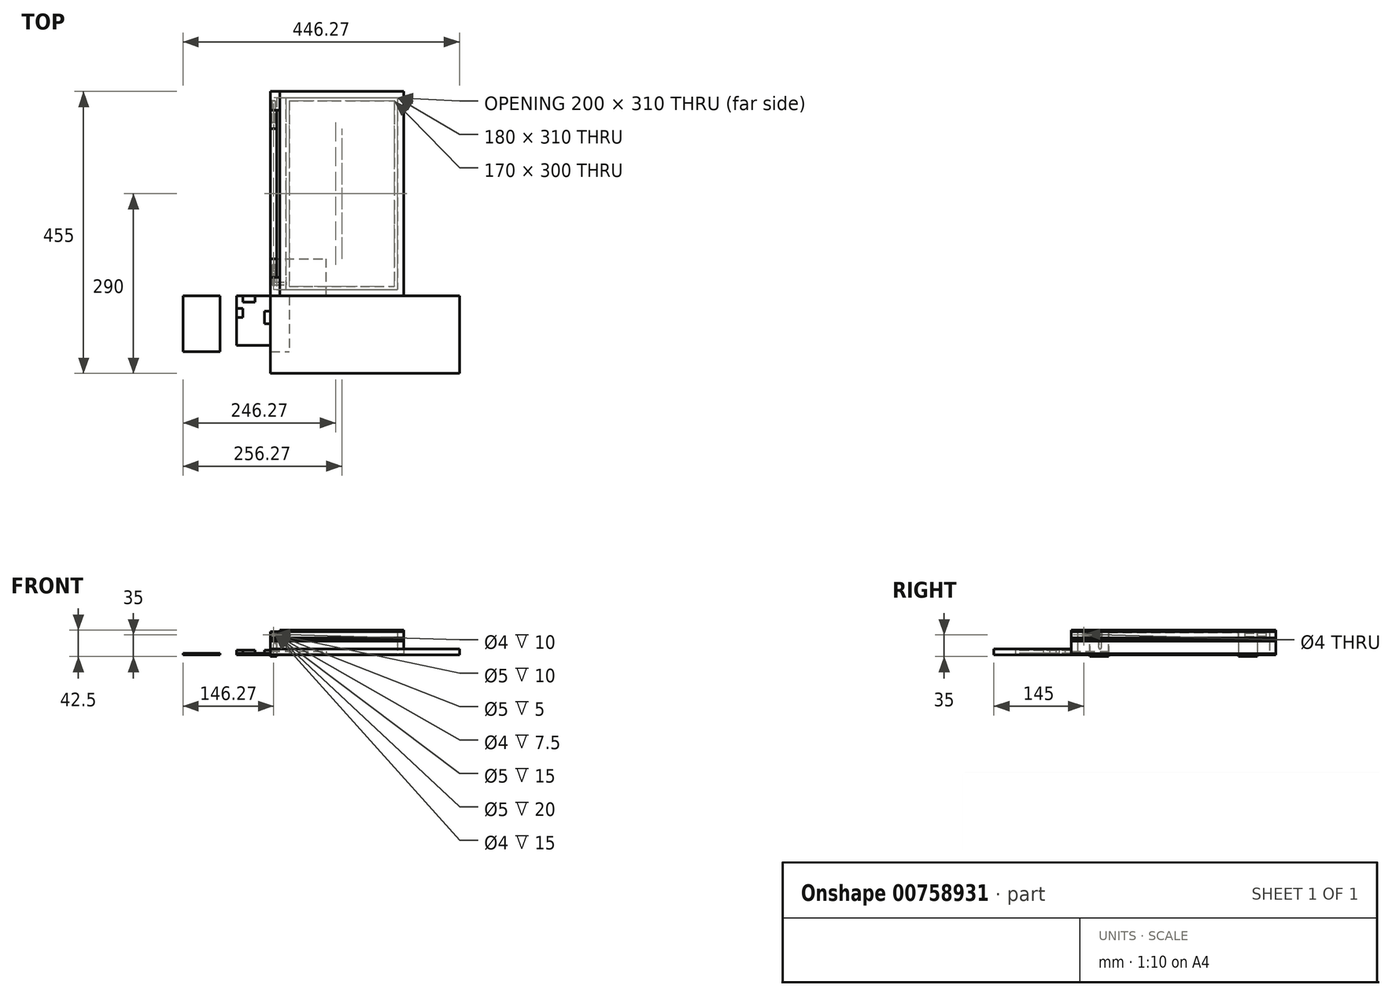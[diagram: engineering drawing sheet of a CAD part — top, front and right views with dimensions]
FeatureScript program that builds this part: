
annotation { "Feature Type Name" : "Feature", "Feature Type Description" : "" }
export const myFeature = defineFeature(function(context is Context, id is Id, definition is map)
    precondition{}
    {
        {
            var Q0;
            Q0=qCreatedBy(makeId("Top.planeOp"),FACE);
            var sketch = newSketch(context, id + "F0", { "sketchPlane" : qUnion([Q0])});
            skLineSegment(sketch, "E0.bottom", {"start": v(0, 0) * mm, "end": v(215, 0) * mm});
            skLineSegment(sketch, "E0.top", {"start": v(0, 330) * mm, "end": v(215, 330) * mm});
            skLineSegment(sketch, "E0.left", {"start": v(0, 0) * mm, "end": v(0, 330) * mm});
            skLineSegment(sketch, "E0.right", {"start": v(215, 0) * mm, "end": v(215, 330) * mm});
            skSolve(sketch);
        }
        {
            var Q0;
            Q0=makeQuery(id+"F0.imprint","IMPRINT",FACE,{"disambiguationData":[TD([[makeQuery(id+"F0.imprint","IMPRINT",EDGE,{"derivedFrom":sQuery(id+"F0.wireOp",EDGE,"E0.bottom")}),1.0]])]});
            extrude(context, id + "F1", {"entities" : qUnion([Q0]), "depth" : 2.5 * mm, "offsetDistance" : 25 * mm});
        }
        {
            var Q0;
            Q0=makeQuery(id+"F1.opExtrude","CAP_FACE",FACE,{"disambiguationData":[OSD([sQuery(id+"F0.wireOp",EDGE,"E0.bottom"),sQuery(id+"F0.wireOp",EDGE,"E0.top"),sQuery(id+"F0.wireOp",EDGE,"E0.left"),sQuery(id+"F0.wireOp",EDGE,"E0.right")])],"isStart":false});
            var sketch = newSketch(context, id + "F2", { "sketchPlane" : qUnion([Q0])});
            skLineSegment(sketch, "E1", {"start": v(215, 0) * mm, "end": v(215, 10) * mm, "construction": true});
            skLineSegment(sketch, "E2", {"start": v(215, 10) * mm, "end": v(205, 10) * mm, "construction": true});
            skLineSegment(sketch, "E3", {"start": v(0, 330) * mm, "end": v(0, 320) * mm, "construction": true});
            skLineSegment(sketch, "E4", {"start": v(0, 320) * mm, "end": v(10, 320) * mm, "construction": true});
            skLineSegment(sketch, "E5.bottom", {"start": v(10, 320) * mm, "end": v(205, 320) * mm});
            skLineSegment(sketch, "E5.top", {"start": v(10, 10) * mm, "end": v(205, 10) * mm});
            skLineSegment(sketch, "E5.left", {"start": v(10, 320) * mm, "end": v(10, 10) * mm});
            skLineSegment(sketch, "E5.right", {"start": v(205, 320) * mm, "end": v(205, 10) * mm});
            skLineSegment(sketch, "E6.bottom", {"start": v(0, 0) * mm, "end": v(215, 0) * mm});
            skLineSegment(sketch, "E6.top", {"start": v(0, 330) * mm, "end": v(215, 330) * mm});
            skLineSegment(sketch, "E6.left", {"start": v(0, 0) * mm, "end": v(0, 330) * mm});
            skLineSegment(sketch, "E6.right", {"start": v(215, 0) * mm, "end": v(215, 330) * mm});
            skSolve(sketch);
        }
        {
            var Q0;
            Q0=qSketchRegion(id+"F2",true);
            extrude(context, id + "F3", {"entities" : qUnion([Q0]), "depth" : 20 * mm, "offsetDistance" : 25 * mm});
        }
        {
            var Q0;
            Q0=qCreatedBy(makeId("Front.planeOp"),FACE);
            var sketch = newSketch(context, id + "F4", { "sketchPlane" : qUnion([Q0])});
            skLineSegment(sketch, "E7", {"start": v(0, 0) * mm, "end": v(0, 2.5) * mm});
            skLineSegment(sketch, "E8", {"start": v(0, 2.5) * mm, "end": v(5, 2.5) * mm});
            skLineSegment(sketch, "E9", {"start": v(5, 2.5) * mm, "end": v(5, 22.5) * mm});
            skLineSegment(sketch, "E10", {"start": v(5, 22.5) * mm, "end": v(0, 22.5) * mm});
            skLineSegment(sketch, "E11", {"start": v(0, 22.5) * mm, "end": v(0, 37.5) * mm});
            skLineSegment(sketch, "E12", {"start": v(0, 37.5) * mm, "end": v(10, 37.5) * mm});
            skLineSegment(sketch, "E13", {"start": v(10, 37.5) * mm, "end": v(10, -2.5) * mm});
            skLineSegment(sketch, "E14", {"start": v(10, -2.5) * mm, "end": v(0, -2.5) * mm});
            skLineSegment(sketch, "E15", {"start": v(0, -2.5) * mm, "end": v(0, 0) * mm});
            skLineSegment(sketch, "E16", {"start": v(5, 37.5) * mm, "end": v(5, 32.5) * mm, "construction": true});
            skCircle(sketch, "E17", {"center": v(5, 32.5) * mm, "radius": 2.5 * mm, "construction": true});
            skSolve(sketch);
        }
        {
            var Q0;
            Q0=qSketchRegion(id+"F4",true);
            extrude(context, id + "F5", {"entities" : qUnion([Q0]), "oppositeDirection" : true, "depth" : 30 * mm, "offsetDistance" : 25 * mm});
        }
        {
            var Q0;
            Q0=makeQuery(id+"F5.opExtrude","SWEPT_BODY",BODY,{"disambiguationData":[OSD([sQuery(id+"F4.wireOp",EDGE,"E7"),sQuery(id+"F4.wireOp",EDGE,"E8"),sQuery(id+"F4.wireOp",EDGE,"E9"),sQuery(id+"F4.wireOp",EDGE,"E10"),sQuery(id+"F4.wireOp",EDGE,"E11"),sQuery(id+"F4.wireOp",EDGE,"E12"),sQuery(id+"F4.wireOp",EDGE,"E13"),sQuery(id+"F4.wireOp",EDGE,"E14"),sQuery(id+"F4.wireOp",EDGE,"E15"),sQuery(id+"F4.wireOp",EDGE,"E17")])]});
            transform(context, id + "F6", {"entities" : qUnion([Q0]), "transformType" : TransformType.TRANSLATION_3D, "dx" : 0 * mm, "dy" : 30 * mm, "dz" : 0 * mm, "makeCopy" : false});
        }
        {
            var Q0;
            Q0=makeQuery(id+"F5.opExtrude","SWEPT_BODY",BODY,{"disambiguationData":[OSD([sQuery(id+"F4.wireOp",EDGE,"E7"),sQuery(id+"F4.wireOp",EDGE,"E8"),sQuery(id+"F4.wireOp",EDGE,"E9"),sQuery(id+"F4.wireOp",EDGE,"E10"),sQuery(id+"F4.wireOp",EDGE,"E11"),sQuery(id+"F4.wireOp",EDGE,"E12"),sQuery(id+"F4.wireOp",EDGE,"E13"),sQuery(id+"F4.wireOp",EDGE,"E14"),sQuery(id+"F4.wireOp",EDGE,"E15"),sQuery(id+"F4.wireOp",EDGE,"E17")])]});
            transform(context, id + "F7", {"entities" : qUnion([Q0]), "transformType" : TransformType.TRANSLATION_3D, "dx" : 0 * mm, "dy" : 240 * mm, "dz" : 0 * mm, "makeCopy" : true});
        }
        {
            var Q0;
            Q0=makeQuery(id+"F3.opExtrude","CAP_FACE",FACE,{"disambiguationData":[OSD([sQuery(id+"F2.wireOp",EDGE,"E5.bottom"),sQuery(id+"F2.wireOp",EDGE,"E5.top"),sQuery(id+"F2.wireOp",EDGE,"E5.left"),sQuery(id+"F2.wireOp",EDGE,"E5.right"),sQuery(id+"F2.wireOp",EDGE,"E6.bottom"),sQuery(id+"F2.wireOp",EDGE,"E6.top"),sQuery(id+"F2.wireOp",EDGE,"E6.left"),sQuery(id+"F2.wireOp",EDGE,"E6.right")])],"isStart":false});
            var sketch = newSketch(context, id + "F8", { "sketchPlane" : qUnion([Q0])});
            skLineSegment(sketch, "E18.bottom", {"start": v(0, 0) * mm, "end": v(215, 0) * mm});
            skLineSegment(sketch, "E18.top", {"start": v(0, 330) * mm, "end": v(215, 330) * mm});
            skLineSegment(sketch, "E18.left", {"start": v(0, 0) * mm, "end": v(0, 330) * mm});
            skLineSegment(sketch, "E18.right", {"start": v(215, 0) * mm, "end": v(215, 330) * mm});
            skSolve(sketch);
        }
        {
            var Q0;
            Q0=qSketchRegion(id+"F8",true);
            extrude(context, id + "F9", {"entities" : qUnion([Q0]), "depth" : 2.5 * mm, "offsetDistance" : 25 * mm});
        }
        {
            var Q0;
            Q0=makeQuery(id+"F7.opPattern","COPY",BODY,{"derivedFrom":makeQuery(id+"F5.opExtrude","SWEPT_BODY",BODY,{"disambiguationData":[OSD([sQuery(id+"F4.wireOp",EDGE,"E7"),sQuery(id+"F4.wireOp",EDGE,"E8"),sQuery(id+"F4.wireOp",EDGE,"E9"),sQuery(id+"F4.wireOp",EDGE,"E10"),sQuery(id+"F4.wireOp",EDGE,"E11"),sQuery(id+"F4.wireOp",EDGE,"E12"),sQuery(id+"F4.wireOp",EDGE,"E13"),sQuery(id+"F4.wireOp",EDGE,"E14"),sQuery(id+"F4.wireOp",EDGE,"E15"),sQuery(id+"F4.wireOp",EDGE,"E17")])]}),"instanceName":"1"});
            var Q1;
            Q1=makeQuery(id+"F5.opExtrude","SWEPT_BODY",BODY,{"disambiguationData":[OSD([sQuery(id+"F4.wireOp",EDGE,"E7"),sQuery(id+"F4.wireOp",EDGE,"E8"),sQuery(id+"F4.wireOp",EDGE,"E9"),sQuery(id+"F4.wireOp",EDGE,"E10"),sQuery(id+"F4.wireOp",EDGE,"E11"),sQuery(id+"F4.wireOp",EDGE,"E12"),sQuery(id+"F4.wireOp",EDGE,"E13"),sQuery(id+"F4.wireOp",EDGE,"E14"),sQuery(id+"F4.wireOp",EDGE,"E15"),sQuery(id+"F4.wireOp",EDGE,"E17")])]});
            var Q2;
            Q2=makeQuery(id+"F3.opExtrude","SWEPT_BODY",BODY,{"disambiguationData":[OSD([sQuery(id+"F2.wireOp",EDGE,"E5.bottom"),sQuery(id+"F2.wireOp",EDGE,"E5.top"),sQuery(id+"F2.wireOp",EDGE,"E5.left"),sQuery(id+"F2.wireOp",EDGE,"E5.right"),sQuery(id+"F2.wireOp",EDGE,"E6.bottom"),sQuery(id+"F2.wireOp",EDGE,"E6.top"),sQuery(id+"F2.wireOp",EDGE,"E6.left"),sQuery(id+"F2.wireOp",EDGE,"E6.right")])]});
            var Q3;
            Q3=makeQuery(id+"F9.opExtrude","SWEPT_BODY",BODY,{"disambiguationData":[OSD([sQuery(id+"F8.wireOp",EDGE,"E18.bottom"),sQuery(id+"F8.wireOp",EDGE,"E18.top"),sQuery(id+"F8.wireOp",EDGE,"E18.left"),sQuery(id+"F8.wireOp",EDGE,"E18.right")])]});
            var Q4;
            Q4=makeQuery(id+"F1.opExtrude","SWEPT_BODY",BODY,{"disambiguationData":[OSD([sQuery(id+"F0.wireOp",EDGE,"E0.bottom"),sQuery(id+"F0.wireOp",EDGE,"E0.top"),sQuery(id+"F0.wireOp",EDGE,"E0.left"),sQuery(id+"F0.wireOp",EDGE,"E0.right")])]});
            booleanBodies(context, id + "F10", {"operationType" : BooleanOperationType.SUBTRACTION, "tools" : qUnion([Q0, Q1]), "targets" : qUnion([Q2, Q3, Q4]), "keepTools" : true});
        }
        {
            var Q0;
            Q0=makeQuery(id+"F9.opExtrude","CAP_FACE",FACE,{"disambiguationData":[OSD([sQuery(id+"F8.wireOp",EDGE,"E18.bottom"),sQuery(id+"F8.wireOp",EDGE,"E18.top"),sQuery(id+"F8.wireOp",EDGE,"E18.left"),sQuery(id+"F8.wireOp",EDGE,"E18.right")])],"isStart":false});
            var sketch = newSketch(context, id + "F11", { "sketchPlane" : qUnion([Q0])});
            skLineSegment(sketch, "E19.bottom", {"start": v(215, 0) * mm, "end": v(15, 0) * mm});
            skLineSegment(sketch, "E19.top", {"start": v(215, 330) * mm, "end": v(15, 330) * mm});
            skLineSegment(sketch, "E19.left", {"start": v(215, 0) * mm, "end": v(215, 330) * mm});
            skLineSegment(sketch, "E19.right", {"start": v(15, 0) * mm, "end": v(15, 330) * mm});
            skLineSegment(sketch, "E20", {"start": v(215, 0) * mm, "end": v(215, 15) * mm, "construction": true});
            skLineSegment(sketch, "E21", {"start": v(215, 15) * mm, "end": v(200, 15) * mm, "construction": true});
            skLineSegment(sketch, "E22", {"start": v(15, 330) * mm, "end": v(15, 315) * mm, "construction": true});
            skLineSegment(sketch, "E23", {"start": v(15, 315) * mm, "end": v(30, 315) * mm, "construction": true});
            skLineSegment(sketch, "E24.bottom", {"start": v(30, 315) * mm, "end": v(200, 315) * mm});
            skLineSegment(sketch, "E24.top", {"start": v(30, 15) * mm, "end": v(200, 15) * mm});
            skLineSegment(sketch, "E24.left", {"start": v(30, 315) * mm, "end": v(30, 15) * mm});
            skLineSegment(sketch, "E24.right", {"start": v(200, 315) * mm, "end": v(200, 15) * mm});
            skSolve(sketch);
        }
        {
            var Q0;
            Q0=qSketchRegion(id+"F11",true);
            extrude(context, id + "F12", {"entities" : qUnion([Q0]), "depth" : 2.5 * mm, "offsetDistance" : 25 * mm});
        }
        {
            var Q0;
            Q0=makeQuery(id+"F12.opExtrude","CAP_FACE",FACE,{"disambiguationData":[OSD([sQuery(id+"F11.wireOp",EDGE,"E19.bottom"),sQuery(id+"F11.wireOp",EDGE,"E19.top"),sQuery(id+"F11.wireOp",EDGE,"E19.left"),sQuery(id+"F11.wireOp",EDGE,"E19.right"),sQuery(id+"F11.wireOp",EDGE,"E24.bottom"),sQuery(id+"F11.wireOp",EDGE,"E24.top"),sQuery(id+"F11.wireOp",EDGE,"E24.left"),sQuery(id+"F11.wireOp",EDGE,"E24.right")])],"isStart":false});
            var sketch = newSketch(context, id + "F13", { "sketchPlane" : qUnion([Q0])});
            skLineSegment(sketch, "E25.bottom", {"start": v(215, 0) * mm, "end": v(0, 0) * mm});
            skLineSegment(sketch, "E25.top", {"start": v(215, 330) * mm, "end": v(0, 330) * mm});
            skLineSegment(sketch, "E25.left", {"start": v(215, 0) * mm, "end": v(215, 330) * mm});
            skLineSegment(sketch, "E25.right", {"start": v(0, 0) * mm, "end": v(0, 330) * mm, "construction": true});
            skLineSegment(sketch, "E26", {"start": v(0, 0) * mm, "end": v(0, 30) * mm});
            skLineSegment(sketch, "E27", {"start": v(0, 30) * mm, "end": v(15, 30) * mm});
            skLineSegment(sketch, "E28", {"start": v(0, 330) * mm, "end": v(0, 300) * mm});
            skLineSegment(sketch, "E29", {"start": v(0, 300) * mm, "end": v(15, 300) * mm});
            skLineSegment(sketch, "E30", {"start": v(15, 300) * mm, "end": v(15, 30) * mm});
            skLineSegment(sketch, "E31", {"start": v(215, 330) * mm, "end": v(215, 320) * mm, "construction": true});
            skLineSegment(sketch, "E32", {"start": v(215, 320) * mm, "end": v(205, 320) * mm, "construction": true});
            skLineSegment(sketch, "E33", {"start": v(15, 30) * mm, "end": v(25, 30) * mm, "construction": true});
            skLineSegment(sketch, "E34", {"start": v(25, 30) * mm, "end": v(25, 10) * mm, "construction": true});
            skLineSegment(sketch, "E35.bottom", {"start": v(25, 10) * mm, "end": v(205, 10) * mm});
            skLineSegment(sketch, "E35.top", {"start": v(25, 320) * mm, "end": v(205, 320) * mm});
            skLineSegment(sketch, "E35.left", {"start": v(25, 10) * mm, "end": v(25, 320) * mm});
            skLineSegment(sketch, "E35.right", {"start": v(205, 10) * mm, "end": v(205, 320) * mm});
            skSolve(sketch);
        }
        {
            var Q0;
            Q0=qSketchRegion(id+"F13",true);
            extrude(context, id + "F14", {"entities" : qUnion([Q0]), "depth" : 10 * mm, "offsetDistance" : 25 * mm});
        }
        {
            var Q0;
            Q0=makeQuery(id+"F14.opExtrude","CAP_FACE",FACE,{"disambiguationData":[OSD([sQuery(id+"F13.wireOp",EDGE,"E25.bottom"),sQuery(id+"F13.wireOp",EDGE,"E25.top"),sQuery(id+"F13.wireOp",EDGE,"E25.left"),sQuery(id+"F13.wireOp",EDGE,"E26"),sQuery(id+"F13.wireOp",EDGE,"E27"),sQuery(id+"F13.wireOp",EDGE,"E28"),sQuery(id+"F13.wireOp",EDGE,"E29"),sQuery(id+"F13.wireOp",EDGE,"E30"),sQuery(id+"F13.wireOp",EDGE,"E35.bottom"),sQuery(id+"F13.wireOp",EDGE,"E35.top"),sQuery(id+"F13.wireOp",EDGE,"E35.left"),sQuery(id+"F13.wireOp",EDGE,"E35.right")])],"isStart":false});
            var sketch = newSketch(context, id + "F15", { "sketchPlane" : qUnion([Q0])});
            skLineSegment(sketch, "E36.bottom", {"start": v(215, 0) * mm, "end": v(15, 0) * mm});
            skLineSegment(sketch, "E36.top", {"start": v(215, 330) * mm, "end": v(15, 330) * mm});
            skLineSegment(sketch, "E36.left", {"start": v(215, 0) * mm, "end": v(215, 330) * mm});
            skLineSegment(sketch, "E36.right", {"start": v(15, 0) * mm, "end": v(15, 330) * mm});
            skSolve(sketch);
        }
        {
            var Q0;
            Q0=qSketchRegion(id+"F15",true);
            extrude(context, id + "F16", {"entities" : qUnion([Q0]), "depth" : 2.5 * mm, "offsetDistance" : 25 * mm});
        }
        {
            var Q0;
            Q0=makeQuery(id+"F7.opPattern","COPY",FACE,{"derivedFrom":makeQuery(id+"F5.opExtrude","CAP_FACE",FACE,{"disambiguationData":[OSD([sQuery(id+"F4.wireOp",EDGE,"E7"),sQuery(id+"F4.wireOp",EDGE,"E8"),sQuery(id+"F4.wireOp",EDGE,"E9"),sQuery(id+"F4.wireOp",EDGE,"E10"),sQuery(id+"F4.wireOp",EDGE,"E11"),sQuery(id+"F4.wireOp",EDGE,"E12"),sQuery(id+"F4.wireOp",EDGE,"E13"),sQuery(id+"F4.wireOp",EDGE,"E14"),sQuery(id+"F4.wireOp",EDGE,"E15"),sQuery(id+"F4.wireOp",EDGE,"E17")])],"isStart":true}),"instanceName":"1"});
            var sketch = newSketch(context, id + "F17", { "sketchPlane" : qUnion([Q0])});
            skLineSegment(sketch, "E37", {"start": v(0, 37.5) * mm, "end": v(0, 25) * mm});
            skLineSegment(sketch, "E38", {"start": v(0, 25) * mm, "end": v(1, 25) * mm});
            skLineSegment(sketch, "E39", {"start": v(1, 25) * mm, "end": v(1, 36.5) * mm});
            skLineSegment(sketch, "E40", {"start": v(1, 36.5) * mm, "end": v(9, 36.5) * mm});
            skLineSegment(sketch, "E41", {"start": v(9, 36.5) * mm, "end": v(9, 25) * mm});
            skLineSegment(sketch, "E42", {"start": v(9, 25) * mm, "end": v(10, 25) * mm});
            skLineSegment(sketch, "E43", {"start": v(10, 25) * mm, "end": v(10, 37.5) * mm});
            skLineSegment(sketch, "E44", {"start": v(10, 37.5) * mm, "end": v(0, 37.5) * mm});
            skSolve(sketch);
        }
        {
            var Q0;
            Q0=qSketchRegion(id+"F17",true);
            extrude(context, id + "F18", {"entities" : qUnion([Q0]), "endBound" : BoundingType.UP_TO_NEXT, "depth" : 25 * mm, "offsetDistance" : 25 * mm});
        }
        {
            var Q0;
            Q0=makeQuery(id+"F14.opExtrude","SWEPT_FACE",FACE,{"disambiguationData":[OSD([sQuery(id+"F13.wireOp",EDGE,"E35.left")])]});
            var sketch = newSketch(context, id + "F19", { "sketchPlane" : qUnion([Q0])});
            skLineSegment(sketch, "E45", {"start": v(10, 32.5) * mm, "end": v(20, 32.5) * mm, "construction": true});
            skCircle(sketch, "E46", {"center": v(20, 32.5) * mm, "radius": 2 * mm});
            skSolve(sketch);
        }
        {
            var Q0;
            Q0=makeQuery(id+"F19.imprint","IMPRINT",FACE,{"disambiguationData":[TD([[makeQuery(id+"F19.imprint","IMPRINT",EDGE,{"derivedFrom":sQuery(id+"F19.wireOp",EDGE,"E46")}),1.0]])]});
            var Q1;
            Q1=sQuery(id+"F19.wireOp",EDGE,"E46");
            extrude(context, id + "F20", {"entities" : qUnion([Q0]), "operationType" : NewBodyOperationType.REMOVE, "surfaceEntities" : qUnion([Q1]), "oppositeDirection" : true, "depth" : 20 * mm, "offsetDistance" : 25 * mm});
        }
        {
            var Q0;
            Q0=makeQuery(id+"F14.opExtrude","SWEPT_FACE",FACE,{"disambiguationData":[OSD([sQuery(id+"F13.wireOp",EDGE,"E27")])]});
            var sketch = newSketch(context, id + "F21", { "sketchPlane" : qUnion([Q0])});
            skLineSegment(sketch, "E47", {"start": v(0, 32.5) * mm, "end": v(-5, 32.5) * mm, "construction": true});
            skCircle(sketch, "E48", {"center": v(-5, 32.5) * mm, "radius": 2.5 * mm});
            skSolve(sketch);
        }
        {
            var Q0;
            Q0=qSketchRegion(id+"F21",true);
            extrude(context, id + "F22", {"entities" : qUnion([Q0]), "operationType" : NewBodyOperationType.REMOVE, "oppositeDirection" : true, "depth" : 5 * mm, "offsetDistance" : 25 * mm});
        }
        {
            var Q0;
            Q0=makeQuery(id+"F22.boolean.opBoolean","COPY",FACE,{"derivedFrom":makeQuery(id+"F22.opExtrude","CAP_FACE",FACE,{"disambiguationData":[OSD([sQuery(id+"F21.wireOp",EDGE,"E48")])],"isStart":false})});
            var sketch = newSketch(context, id + "F23", { "sketchPlane" : qUnion([Q0])});
            skCircle(sketch, "E49", {"center": v(-5, 32.5) * mm, "radius": 2 * mm});
            skSolve(sketch);
        }
        {
            var Q0;
            Q0=qSketchRegion(id+"F23",true);
            extrude(context, id + "F24", {"entities" : qUnion([Q0]), "operationType" : NewBodyOperationType.REMOVE, "oppositeDirection" : true, "depth" : 7.5 * mm, "offsetDistance" : 25 * mm});
        }
        {
            var Q0;
            Q0=makeQuery(id+"F5.opExtrude","CAP_FACE",FACE,{"disambiguationData":[OSD([sQuery(id+"F4.wireOp",EDGE,"E7"),sQuery(id+"F4.wireOp",EDGE,"E8"),sQuery(id+"F4.wireOp",EDGE,"E9"),sQuery(id+"F4.wireOp",EDGE,"E10"),sQuery(id+"F4.wireOp",EDGE,"E11"),sQuery(id+"F4.wireOp",EDGE,"E12"),sQuery(id+"F4.wireOp",EDGE,"E13"),sQuery(id+"F4.wireOp",EDGE,"E14"),sQuery(id+"F4.wireOp",EDGE,"E15")])],"isStart":true});
            var sketch = newSketch(context, id + "F25", { "sketchPlane" : qUnion([Q0])});
            skLineSegment(sketch, "E50", {"start": v(5, 37.5) * mm, "end": v(5, 32.5) * mm, "construction": true});
            skCircle(sketch, "E51", {"center": v(5, 32.5) * mm, "radius": 2.5 * mm});
            skSolve(sketch);
        }
        {
            var Q0;
            Q0=qSketchRegion(id+"F25",true);
            extrude(context, id + "F26", {"entities" : qUnion([Q0]), "operationType" : NewBodyOperationType.REMOVE, "oppositeDirection" : true, "depth" : 10 * mm, "offsetDistance" : 25 * mm});
        }
        {
            var Q0;
            Q0=makeQuery(id+"F26.boolean.opBoolean","COPY",FACE,{"derivedFrom":makeQuery(id+"F26.opExtrude","CAP_FACE",FACE,{"disambiguationData":[OSD([sQuery(id+"F25.wireOp",EDGE,"E51")])],"isStart":false})});
            var sketch = newSketch(context, id + "F27", { "sketchPlane" : qUnion([Q0])});
            skCircle(sketch, "E52", {"center": v(5, 32.5) * mm, "radius": 2 * mm});
            skSolve(sketch);
        }
        {
            var Q0;
            Q0=makeQuery(id+"F27.imprint","IMPRINT",FACE,{"disambiguationData":[TD([[makeQuery(id+"F27.imprint","IMPRINT",EDGE,{"derivedFrom":sQuery(id+"F27.wireOp",EDGE,"E52")}),1.0]])]});
            extrude(context, id + "F28", {"entities" : qUnion([Q0]), "operationType" : NewBodyOperationType.REMOVE, "oppositeDirection" : true, "depth" : 10 * mm, "offsetDistance" : 25 * mm});
        }
        {
            var Q0;
            Q0=makeQuery(id+"F26.boolean.opBoolean","COPY",FACE,{"derivedFrom":makeQuery(id+"F26.opExtrude","CAP_FACE",FACE,{"disambiguationData":[OSD([sQuery(id+"F25.wireOp",EDGE,"E51")])],"isStart":false})});
            extrude(context, id + "F29", {"entities" : qUnion([Q0]), "depth" : 15 * mm, "offsetDistance" : 25 * mm});
        }
        {
            var Q0;
            Q0=qCreatedBy(makeId("Top.planeOp"),FACE);
            var sketch = newSketch(context, id + "F30", { "sketchPlane" : qUnion([Q0])});
            skCircle(sketch, "E53", {"center": v(0, -3.6) * mm, "radius": 2 * mm});
            skSolve(sketch);
        }
        {
            var Q0;
            Q0=qSketchRegion(id+"F30",true);
            extrude(context, id + "F31", {"entities" : qUnion([Q0]), "depth" : 30 * mm, "offsetDistance" : 25 * mm});
        }
        {
            var Q0;
            Q0=makeQuery(id+"F31.opExtrude","SWEPT_BODY",BODY,{"disambiguationData":[OSD([sQuery(id+"F30.wireOp",EDGE,"E53")])]});
            transform(context, id + "F32", {"entities" : qUnion([Q0]), "transformType" : TransformType.TRANSLATION_3D, "dx" : 10 * mm, "dy" : 50 * mm, "dz" : 0 * mm, "makeCopy" : false});
        }
        {
            var Q0;
            Q0=makeQuery(id+"F31.opExtrude","SWEPT_BODY",BODY,{"disambiguationData":[OSD([sQuery(id+"F30.wireOp",EDGE,"E53")])]});
            var Q1;
            Q1=makeQuery(id+"F5.opExtrude","SWEPT_EDGE",EDGE,{"disambiguationData":[OSD([sQuery(id+"F4.wireOp",EDGE,"E9"),sQuery(id+"F4.wireOp",EDGE,"E10")])]});
            transform(context, id + "F33", {"entities" : qUnion([Q0]), "transformType" : TransformType.ROTATION, "transformAxis" : qUnion([Q1]), "angle" : 17 * degree, "makeCopy" : false});
        }
        {
            var Q0;
            Q0=makeQuery(id+"F31.opExtrude","SWEPT_BODY",BODY,{"disambiguationData":[OSD([sQuery(id+"F30.wireOp",EDGE,"E53")])]});
            transform(context, id + "F34", {"entities" : qUnion([Q0]), "transformType" : TransformType.TRANSLATION_3D, "dx" : -2.6 * mm, "dy" : 0 * mm, "dz" : 1.4 * mm, "makeCopy" : false});
        }
        {
            var Q0;
            Q0=makeQuery(id+"F31.opExtrude","SWEPT_BODY",BODY,{"disambiguationData":[OSD([sQuery(id+"F30.wireOp",EDGE,"E53")])]});
            var Q1;
            Q1=makeQuery(id+"F5.opExtrude","SWEPT_BODY",BODY,{"disambiguationData":[OSD([sQuery(id+"F4.wireOp",EDGE,"E7"),sQuery(id+"F4.wireOp",EDGE,"E8"),sQuery(id+"F4.wireOp",EDGE,"E9"),sQuery(id+"F4.wireOp",EDGE,"E10"),sQuery(id+"F4.wireOp",EDGE,"E11"),sQuery(id+"F4.wireOp",EDGE,"E12"),sQuery(id+"F4.wireOp",EDGE,"E13"),sQuery(id+"F4.wireOp",EDGE,"E14"),sQuery(id+"F4.wireOp",EDGE,"E15")])]});
            booleanBodies(context, id + "F35", {"operationType" : BooleanOperationType.SUBTRACTION, "tools" : qUnion([Q0]), "targets" : qUnion([Q1])});
        }
        {
            var Q0;
            Q0=makeQuery(id+"F7.opPattern","COPY",FACE,{"derivedFrom":makeQuery(id+"F5.opExtrude","CAP_FACE",FACE,{"disambiguationData":[OSD([sQuery(id+"F4.wireOp",EDGE,"E7"),sQuery(id+"F4.wireOp",EDGE,"E8"),sQuery(id+"F4.wireOp",EDGE,"E9"),sQuery(id+"F4.wireOp",EDGE,"E10"),sQuery(id+"F4.wireOp",EDGE,"E11"),sQuery(id+"F4.wireOp",EDGE,"E12"),sQuery(id+"F4.wireOp",EDGE,"E13"),sQuery(id+"F4.wireOp",EDGE,"E14"),sQuery(id+"F4.wireOp",EDGE,"E15")])],"isStart":false}),"instanceName":"1"});
            var sketch = newSketch(context, id + "F36", { "sketchPlane" : qUnion([Q0])});
            skLineSegment(sketch, "E54", {"start": v(-5, 37.5) * mm, "end": v(-5, 32.5) * mm, "construction": true});
            skCircle(sketch, "E55", {"center": v(-5, 32.5) * mm, "radius": 2.5 * mm});
            skSolve(sketch);
        }
        {
            var Q0;
            Q0=qSketchRegion(id+"F36",true);
            extrude(context, id + "F37", {"entities" : qUnion([Q0]), "operationType" : NewBodyOperationType.REMOVE, "oppositeDirection" : true, "depth" : 20 * mm, "offsetDistance" : 25 * mm});
        }
        {
            var Q0;
            Q0=makeQuery(id+"F14.opExtrude","SWEPT_FACE",FACE,{"disambiguationData":[OSD([sQuery(id+"F13.wireOp",EDGE,"E29")])]});
            var sketch = newSketch(context, id + "F38", { "sketchPlane" : qUnion([Q0])});
            skLineSegment(sketch, "E56", {"start": v(0, 32.5) * mm, "end": v(5, 32.5) * mm, "construction": true});
            skCircle(sketch, "E57", {"center": v(5, 32.5) * mm, "radius": 2.5 * mm});
            skSolve(sketch);
        }
        {
            var Q0;
            Q0=qSketchRegion(id+"F38",true);
            extrude(context, id + "F39", {"entities" : qUnion([Q0]), "operationType" : NewBodyOperationType.REMOVE, "oppositeDirection" : true, "depth" : 15 * mm, "offsetDistance" : 25 * mm});
        }
        {
            var Q0;
            Q0=qCreatedBy(makeId("Top.planeOp"),FACE);
            var sketch = newSketch(context, id + "F40", { "sketchPlane" : qUnion([Q0])});
            skLineSegment(sketch, "E58.bottom", {"start": v(0, 0) * mm, "end": v(90, 0) * mm});
            skLineSegment(sketch, "E58.top", {"start": v(0, 60) * mm, "end": v(90, 60) * mm});
            skLineSegment(sketch, "E58.left", {"start": v(0, 0) * mm, "end": v(0, 60) * mm});
            skLineSegment(sketch, "E58.right", {"start": v(90, 0) * mm, "end": v(90, 60) * mm});
            skSolve(sketch);
        }
        {
            var Q0;
            Q0 = qSketchRegion(id + "F40", true);
            extrude(context, id + "F41", {"entities" : qUnion([Q0]), "depth" : 6 * mm, "offsetDistance" : 25 * mm});
        }
        {
            var Q0;
            Q0=qCreatedBy(makeId("Top.planeOp"),FACE);
            var sketch = newSketch(context, id + "F42", { "sketchPlane" : qUnion([Q0])});
            skLineSegment(sketch, "E59.bottom", {"start": v(0, 0) * mm, "end": v(30, 0) * mm});
            skLineSegment(sketch, "E59.top", {"start": v(0, -90) * mm, "end": v(30, -90) * mm});
            skLineSegment(sketch, "E59.left", {"start": v(0, 0) * mm, "end": v(0, -90) * mm});
            skLineSegment(sketch, "E59.right", {"start": v(30, 0) * mm, "end": v(30, -90) * mm});
            skSolve(sketch);
        }
        {
            var Q0;
            Q0 = qSketchRegion(id + "F42", true);
            extrude(context, id + "F43", {"entities" : qUnion([Q0]), "depth" : 7 * mm, "offsetDistance" : 25 * mm});
        }
        {
            var Q0;
            Q0=qCreatedBy(makeId("Top.planeOp"),FACE);
            var sketch = newSketch(context, id + "F44", { "sketchPlane" : qUnion([Q0])});
            skLineSegment(sketch, "E60.bottom", {"start": v(0, 0) * mm, "end": v(-55, 0) * mm});
            skLineSegment(sketch, "E60.top", {"start": v(0, -80) * mm, "end": v(-55, -80) * mm});
            skLineSegment(sketch, "E60.left", {"start": v(0, 0) * mm, "end": v(0, -80) * mm});
            skLineSegment(sketch, "E60.right", {"start": v(-55, 0) * mm, "end": v(-55, -80) * mm});
            skSolve(sketch);
        }
        {
            var Q0;
            Q0=makeQuery(id+"F44.imprint","IMPRINT",FACE,{"disambiguationData":[TD([[makeQuery(id+"F44.imprint","IMPRINT",EDGE,{"derivedFrom":sQuery(id+"F44.wireOp",EDGE,"E60.bottom")}),1.0]])]});
            extrude(context, id + "F45", {"entities" : qUnion([Q0]), "depth" : 3 * mm, "offsetDistance" : 25 * mm});
        }
        {
            var Q0;
            Q0=makeQuery(id+"F45.opExtrude","CAP_FACE",FACE,{"disambiguationData":[OSD([sQuery(id+"F44.wireOp",EDGE,"E60.bottom"),sQuery(id+"F44.wireOp",EDGE,"E60.top"),sQuery(id+"F44.wireOp",EDGE,"E60.left"),sQuery(id+"F44.wireOp",EDGE,"E60.right")])],"isStart":false});
            var sketch = newSketch(context, id + "F46", { "sketchPlane" : qUnion([Q0])});
            skLineSegment(sketch, "E61", {"start": v(-55, 0) * mm, "end": v(-45, 0) * mm, "construction": true});
            skLineSegment(sketch, "E62", {"start": v(-55, 0) * mm, "end": v(-55, -20) * mm, "construction": true});
            skLineSegment(sketch, "E63.bottom", {"start": v(-45, 0) * mm, "end": v(-25, 0) * mm});
            skLineSegment(sketch, "E63.top", {"start": v(-45, -10) * mm, "end": v(-25, -10) * mm});
            skLineSegment(sketch, "E63.left", {"start": v(-45, 0) * mm, "end": v(-45, -10) * mm});
            skLineSegment(sketch, "E63.right", {"start": v(-25, 0) * mm, "end": v(-25, -10) * mm});
            skLineSegment(sketch, "E64.bottom", {"start": v(-55, -20) * mm, "end": v(-45, -20) * mm});
            skLineSegment(sketch, "E64.top", {"start": v(-55, -35) * mm, "end": v(-45, -35) * mm});
            skLineSegment(sketch, "E64.left", {"start": v(-55, -20) * mm, "end": v(-55, -35) * mm});
            skLineSegment(sketch, "E64.right", {"start": v(-45, -20) * mm, "end": v(-45, -35) * mm});
            skLineSegment(sketch, "E65", {"start": v(0, 0) * mm, "end": v(0, -25) * mm, "construction": true});
            skLineSegment(sketch, "E66.bottom", {"start": v(0, -25) * mm, "end": v(-10, -25) * mm});
            skLineSegment(sketch, "E66.top", {"start": v(0, -45) * mm, "end": v(-10, -45) * mm});
            skLineSegment(sketch, "E66.left", {"start": v(0, -25) * mm, "end": v(0, -45) * mm});
            skLineSegment(sketch, "E66.right", {"start": v(-10, -25) * mm, "end": v(-10, -45) * mm});
            skSolve(sketch);
        }
        {
            var Q0;
            Q0 = qSketchRegion(id + "F46", true);
            extrude(context, id + "F47", {"entities" : qUnion([Q0]), "operationType" : NewBodyOperationType.ADD, "depth" : 5 * mm, "offsetDistance" : 25 * mm});
        }
        {
            var Q0;
            Q0=qCreatedBy(makeId("Top.planeOp"),FACE);
            var sketch = newSketch(context, id + "F48", { "sketchPlane" : qUnion([Q0])});
            skLineSegment(sketch, "E67.bottom", {"start": v(0, 0) * mm, "end": v(305, 0) * mm});
            skLineSegment(sketch, "E67.top", {"start": v(0, -125) * mm, "end": v(305, -125) * mm});
            skLineSegment(sketch, "E67.left", {"start": v(0, 0) * mm, "end": v(0, -125) * mm});
            skLineSegment(sketch, "E67.right", {"start": v(305, 0) * mm, "end": v(305, -125) * mm});
            skSolve(sketch);
        }
        {
            var Q0;
            Q0=makeQuery(id+"F48.imprint","IMPRINT",FACE,{"disambiguationData":[TD([[makeQuery(id+"F48.imprint","IMPRINT",EDGE,{"derivedFrom":sQuery(id+"F48.wireOp",EDGE,"E67.bottom")}),-1.0]])]});
            extrude(context, id + "F49", {"entities" : qUnion([Q0]), "depth" : 10 * mm, "offsetDistance" : 25 * mm});
        }
        {
            var Q0;
            Q0=qCreatedBy(makeId("Top.planeOp"),FACE);
            var sketch = newSketch(context, id + "F50", { "sketchPlane" : qUnion([Q0])});
            skLineSegment(sketch, "E68.bottom", {"start": v(-141.27, 0) * mm, "end": v(-81.27, 0) * mm});
            skLineSegment(sketch, "E68.top", {"start": v(-141.27, -90) * mm, "end": v(-81.27, -90) * mm});
            skLineSegment(sketch, "E68.left", {"start": v(-141.27, 0) * mm, "end": v(-141.27, -90) * mm});
            skLineSegment(sketch, "E68.right", {"start": v(-81.27, 0) * mm, "end": v(-81.27, -90) * mm});
            skSolve(sketch);
        }
        {
            var Q0;
            Q0 = qSketchRegion(id + "F50", true);
            extrude(context, id + "F51", {"entities" : qUnion([Q0]), "depth" : 3 * mm, "offsetDistance" : 25 * mm});
        }
    });
